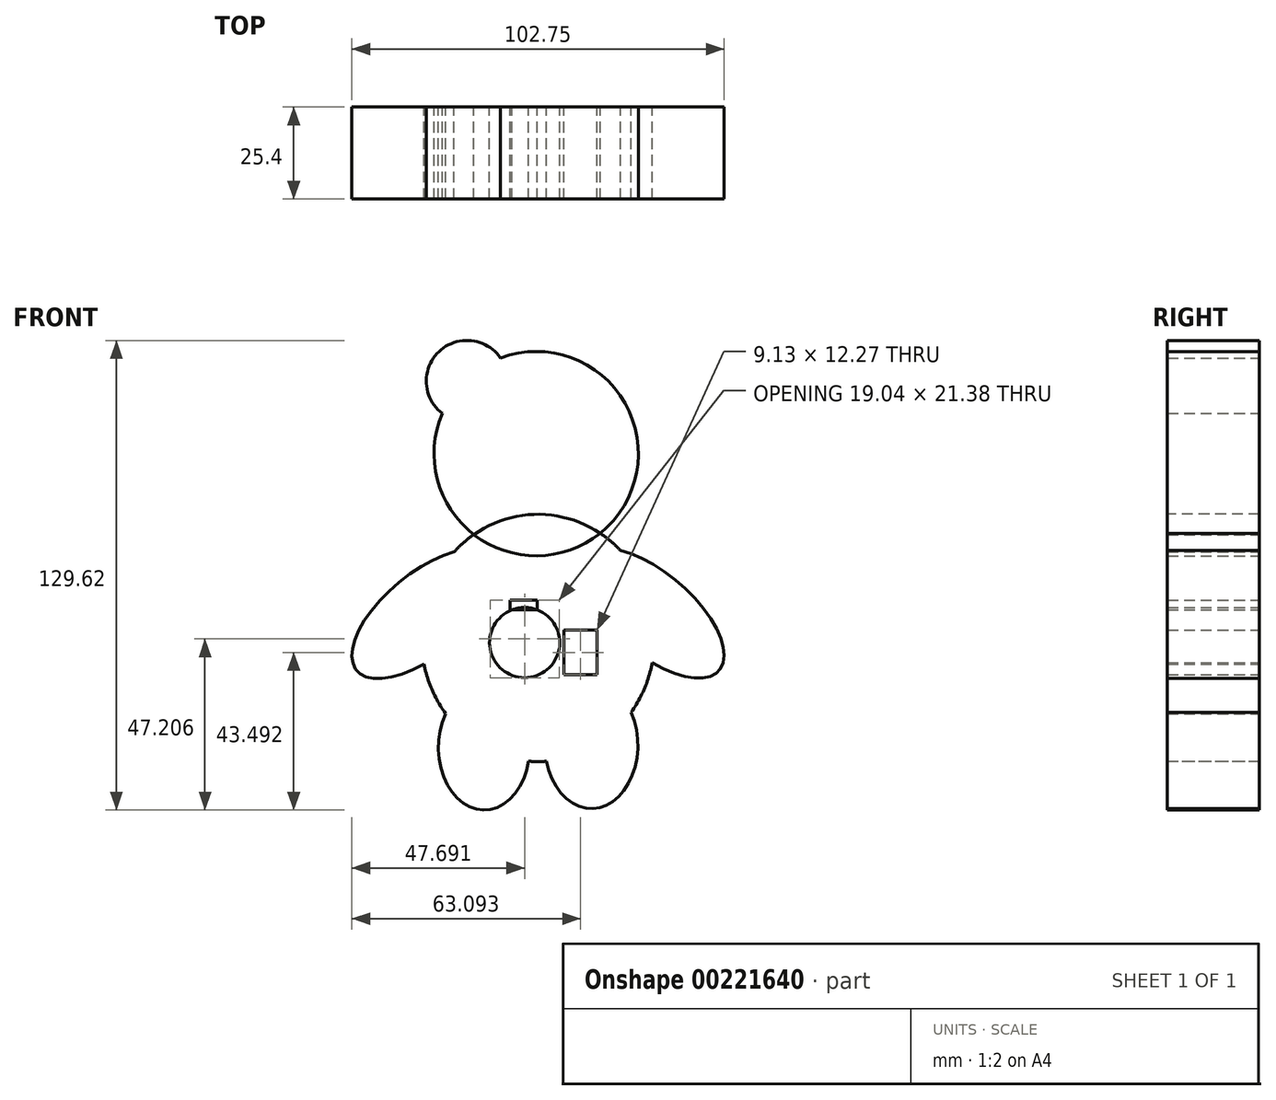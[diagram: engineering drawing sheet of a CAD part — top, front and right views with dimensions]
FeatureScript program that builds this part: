
annotation { "Feature Type Name" : "Feature", "Feature Type Description" : "" }
export const myFeature = defineFeature(function(context is Context, id is Id, definition is map)
    precondition{}
    {
        {
            var Q0;
            Q0=qCreatedBy(makeId("Front.planeOp"),FACE);
            var sketch = newSketch(context, id + "F0", { "sketchPlane" : qUnion([Q0])});
            skCircle(sketch, "E0", {"center": v(3.75, 21.78) * mm, "radius": 28.2 * mm});
            skCircle(sketch, "E1", {"center": v(-15.3, 41.8) * mm, "radius": 11.24 * mm});
            skCircle(sketch, "E2", {"center": v(21.86, 40.85) * mm, "radius": 11.48 * mm});
            skEllipse(sketch, "E3", {"center": v(4.25, -29.08) * mm, "majorRadius": 34.13 * mm, "minorRadius": 32.2 * mm, "majorAxis": v(0, -1)});
            skEllipse(sketch, "E4", {"center": v(-10.63, -59.35) * mm, "majorRadius": 17.23 * mm, "minorRadius": 12.63 * mm, "majorAxis": v(0, -1)});
            skEllipse(sketch, "E5", {"center": v(19, -58.66) * mm, "majorRadius": 17.51 * mm, "minorRadius": 12.83 * mm, "majorAxis": v(0, -1)});
            skEllipse(sketch, "E6", {"center": v(-26.89, -22.46) * mm, "majorRadius": 24.5 * mm, "minorRadius": 11.3 * mm, "majorAxis": v(-0.77, -0.64)});
            skEllipse(sketch, "E7", {"center": v(35.87, -22.32) * mm, "majorRadius": 24.19 * mm, "minorRadius": 11.16 * mm, "majorAxis": v(-0.76, 0.65)});
            skCircle(sketch, "E8", {"center": v(0.57, -30.38) * mm, "radius": 9.69 * mm});
            skLineSegment(sketch, "E9.bottom", {"start": v(-3.42, -18.68) * mm, "end": v(4.07, -18.68) * mm});
            skLineSegment(sketch, "E9.top", {"start": v(-3.42, -21.35) * mm, "end": v(4.07, -21.35) * mm});
            skLineSegment(sketch, "E9.left", {"start": v(-3.42, -18.68) * mm, "end": v(-3.42, -21.35) * mm});
            skLineSegment(sketch, "E9.right", {"start": v(4.07, -18.68) * mm, "end": v(4.07, -21.35) * mm});
            skFitSpline(sketch, "E10", {"points": [v(0, -18.68) * mm, v(4.07, -12.7) * mm, v(9.7, -12.98) * mm], "startDerivative": vector(6.5, 14.43) * mm, "endDerivative": vector(13.03, -3.4) * mm});
            skLineSegment(sketch, "E11.bottom", {"start": v(11.4, -26.96) * mm, "end": v(20.54, -26.96) * mm});
            skLineSegment(sketch, "E11.top", {"start": v(11.4, -39.22) * mm, "end": v(20.54, -39.22) * mm});
            skLineSegment(sketch, "E11.left", {"start": v(11.4, -26.96) * mm, "end": v(11.4, -39.22) * mm});
            skLineSegment(sketch, "E11.right", {"start": v(20.54, -26.96) * mm, "end": v(20.54, -39.22) * mm});
            skPoint(sketch, "E12.1.internal.snap0", {"position": v(0.32, -21.35) * mm});
            skPoint(sketch, "E12.2.internal.snap0", {"position": v(0.32, -21.35) * mm});
            skPoint(sketch, "E12.3.internal.snap0", {"position": v(0.32, -21.35) * mm});
            skPoint(sketch, "E12.4.internal.snap0", {"position": v(0.32, -21.35) * mm});
            skFitSpline(sketch, "E12", {"points": [v(7.7, -23.82) * mm, v(9.98, -21.35) * mm, v(12.27, -21.35) * mm, v(13.4, -21.35) * mm, v(13.7, -21.35) * mm], "startDerivative": vector(5.66, 8.66) * mm, "endDerivative": vector(2.27, -0.06) * mm});
            skFitSpline(sketch, "E13", {"points": [v(14.83, -23.82) * mm, v(15.97, -26.96) * mm], "startDerivative": vector(1.14, -3.14) * mm, "endDerivative": vector(1.14, -3.14) * mm});
            skSolve(sketch);
        }
        {
            var Q0;
            {var subQ1=sQuery(id+"F0.wireOp",EDGE,"E0");var subQ7=sQuery(id+"F0.wireOp",EDGE,"E2");var subQ9=makeQuery(id+"F0.imprint","INTERSECT",VERTEX,{"disambiguationData":[OD(0.0)],"derivedFrom":[subQ1,subQ7]});Q0=makeQuery(id+"F0.imprint","IMPRINT",FACE,{"disambiguationData":[TD([[makeQuery(id+"F0.imprint","IMPRINT",EDGE,{"disambiguationData":[TD([[subQ9,-1.0]])],"derivedFrom":subQ1}),1.0]])]});}
            var Q1;
            {var subQ0=sQuery(id+"F0.wireOp",EDGE,"E4");var subQ1=sQuery(id+"F0.wireOp",EDGE,"E3");var subQ2=makeQuery(id+"F0.imprint","INTERSECT",VERTEX,{"disambiguationData":[OD(0.0)],"derivedFrom":[subQ1,subQ0]});Q1=makeQuery(id+"F0.imprint","IMPRINT",FACE,{"disambiguationData":[TD([[makeQuery(id+"F0.imprint","IMPRINT",EDGE,{"disambiguationData":[TD([[subQ2,-1.0]])],"derivedFrom":subQ1}),1.0]])]});}
            var Q2;
            {var subQ0=sQuery(id+"F0.wireOp",EDGE,"E2");var subQ1=sQuery(id+"F0.wireOp",EDGE,"E0");var subQ2=makeQuery(id+"F0.imprint","INTERSECT",VERTEX,{"disambiguationData":[OD(0.0)],"derivedFrom":[subQ1,subQ0]});Q2=makeQuery(id+"F0.imprint","IMPRINT",FACE,{"disambiguationData":[TD([[makeQuery(id+"F0.imprint","IMPRINT",EDGE,{"disambiguationData":[TD([[subQ2,1.0]])],"derivedFrom":subQ1}),-1.0]])]});}
            var Q3;
            {var subQ0=sQuery(id+"F0.wireOp",EDGE,"E1");var subQ1=sQuery(id+"F0.wireOp",EDGE,"E0");var subQ2=makeQuery(id+"F0.imprint","INTERSECT",VERTEX,{"disambiguationData":[OD(0.0)],"derivedFrom":[subQ1,subQ0]});Q3=makeQuery(id+"F0.imprint","IMPRINT",FACE,{"disambiguationData":[TD([[makeQuery(id+"F0.imprint","IMPRINT",EDGE,{"disambiguationData":[TD([[subQ2,-1.0]])],"derivedFrom":subQ1}),-1.0]])]});}
            var Q4;
            {var subQ0=sQuery(id+"F0.wireOp",EDGE,"E5");var subQ1=sQuery(id+"F0.wireOp",EDGE,"E3");var subQ2=makeQuery(id+"F0.imprint","INTERSECT",VERTEX,{"disambiguationData":[OD(0.0)],"derivedFrom":[subQ1,subQ0]});Q4=makeQuery(id+"F0.imprint","IMPRINT",FACE,{"disambiguationData":[TD([[makeQuery(id+"F0.imprint","IMPRINT",EDGE,{"disambiguationData":[TD([[subQ2,1.0]])],"derivedFrom":subQ1}),-1.0]])]});}
            var Q5;
            {var subQ0=sQuery(id+"F0.wireOp",EDGE,"E4");var subQ1=sQuery(id+"F0.wireOp",EDGE,"E3");var subQ2=makeQuery(id+"F0.imprint","INTERSECT",VERTEX,{"disambiguationData":[OD(0.0)],"derivedFrom":[subQ1,subQ0]});Q5=makeQuery(id+"F0.imprint","IMPRINT",FACE,{"disambiguationData":[TD([[makeQuery(id+"F0.imprint","IMPRINT",EDGE,{"disambiguationData":[TD([[subQ2,-1.0]])],"derivedFrom":subQ1}),-1.0]])]});}
            var Q6;
            {var subQ0=sQuery(id+"F0.wireOp",EDGE,"E2");var subQ1=sQuery(id+"F0.wireOp",EDGE,"E0");var subQ2=makeQuery(id+"F0.imprint","INTERSECT",VERTEX,{"disambiguationData":[OD(0.0)],"derivedFrom":[subQ1,subQ0]});Q6=makeQuery(id+"F0.imprint","IMPRINT",FACE,{"disambiguationData":[TD([[makeQuery(id+"F0.imprint","IMPRINT",EDGE,{"disambiguationData":[TD([[subQ2,1.0]])],"derivedFrom":subQ1}),1.0]])]});}
            var Q7;
            {var subQ0=sQuery(id+"F0.wireOp",EDGE,"E1");var subQ1=sQuery(id+"F0.wireOp",EDGE,"E0");var subQ2=makeQuery(id+"F0.imprint","INTERSECT",VERTEX,{"disambiguationData":[OD(0.0)],"derivedFrom":[subQ1,subQ0]});Q7=makeQuery(id+"F0.imprint","IMPRINT",FACE,{"disambiguationData":[TD([[makeQuery(id+"F0.imprint","IMPRINT",EDGE,{"disambiguationData":[TD([[subQ2,-1.0]])],"derivedFrom":subQ1}),1.0]])]});}
            var Q8;
            {var subQ0=sQuery(id+"F0.wireOp",EDGE,"E3");var subQ1=sQuery(id+"F0.wireOp",EDGE,"E0");var subQ2=makeQuery(id+"F0.imprint","INTERSECT",VERTEX,{"disambiguationData":[OD(0.0)],"derivedFrom":[subQ1,subQ0]});Q8=makeQuery(id+"F0.imprint","IMPRINT",FACE,{"disambiguationData":[TD([[makeQuery(id+"F0.imprint","IMPRINT",EDGE,{"disambiguationData":[TD([[subQ2,-1.0]])],"derivedFrom":subQ1}),1.0]])]});}
            var Q9;
            {var subQ0=sQuery(id+"F0.wireOp",EDGE,"E5");var subQ1=sQuery(id+"F0.wireOp",EDGE,"E3");var subQ2=makeQuery(id+"F0.imprint","INTERSECT",VERTEX,{"disambiguationData":[OD(0.0)],"derivedFrom":[subQ1,subQ0]});Q9=makeQuery(id+"F0.imprint","IMPRINT",FACE,{"disambiguationData":[TD([[makeQuery(id+"F0.imprint","IMPRINT",EDGE,{"disambiguationData":[TD([[subQ2,1.0]])],"derivedFrom":subQ1}),1.0]])]});}
            var Q10;
            {var subQ0=sQuery(id+"F0.wireOp",EDGE,"E7");var subQ1=sQuery(id+"F0.wireOp",EDGE,"E3");var subQ2=makeQuery(id+"F0.imprint","INTERSECT",VERTEX,{"disambiguationData":[OD(0.0)],"derivedFrom":[subQ1,subQ0]});Q10=makeQuery(id+"F0.imprint","IMPRINT",FACE,{"disambiguationData":[TD([[makeQuery(id+"F0.imprint","IMPRINT",EDGE,{"disambiguationData":[TD([[subQ2,-1.0]])],"derivedFrom":subQ1}),1.0]])]});}
            var Q11;
            {var subQ0=sQuery(id+"F0.wireOp",EDGE,"E6");var subQ1=sQuery(id+"F0.wireOp",EDGE,"E3");var subQ2=makeQuery(id+"F0.imprint","INTERSECT",VERTEX,{"disambiguationData":[OD(0.0)],"derivedFrom":[subQ1,subQ0]});Q11=makeQuery(id+"F0.imprint","IMPRINT",FACE,{"disambiguationData":[TD([[makeQuery(id+"F0.imprint","IMPRINT",EDGE,{"disambiguationData":[TD([[subQ2,-1.0]])],"derivedFrom":subQ1}),1.0]])]});}
            var Q12;
            {var subQ0=sQuery(id+"F0.wireOp",EDGE,"E9.top");var subQ1=sQuery(id+"F0.wireOp",EDGE,"E8");var subQ3=makeQuery(id+"F0.imprint","INTERSECT",VERTEX,{"derivedFrom":[subQ1,subQ0]});Q12=makeQuery(id+"F0.imprint","IMPRINT",FACE,{"disambiguationData":[TD([[makeQuery(id+"F0.imprint","IMPRINT",EDGE,{"disambiguationData":[TD([[subQ3,1.0]])],"derivedFrom":subQ1}),1.0]])]});}
            var Q13;
            {var subQ0=sQuery(id+"F0.wireOp",EDGE,"E6");var subQ1=sQuery(id+"F0.wireOp",EDGE,"E3");var subQ2=makeQuery(id+"F0.imprint","INTERSECT",VERTEX,{"disambiguationData":[OD(0.0)],"derivedFrom":[subQ1,subQ0]});Q13=makeQuery(id+"F0.imprint","IMPRINT",FACE,{"disambiguationData":[TD([[makeQuery(id+"F0.imprint","IMPRINT",EDGE,{"disambiguationData":[TD([[subQ2,-1.0]])],"derivedFrom":subQ1}),-1.0]])]});}
            var Q14;
            {var subQ0=sQuery(id+"F0.wireOp",EDGE,"E7");var subQ1=sQuery(id+"F0.wireOp",EDGE,"E3");var subQ2=makeQuery(id+"F0.imprint","INTERSECT",VERTEX,{"disambiguationData":[OD(0.0)],"derivedFrom":[subQ1,subQ0]});Q14=makeQuery(id+"F0.imprint","IMPRINT",FACE,{"disambiguationData":[TD([[makeQuery(id+"F0.imprint","IMPRINT",EDGE,{"disambiguationData":[TD([[subQ2,-1.0]])],"derivedFrom":subQ1}),-1.0]])]});}
            var Q15;
            {var subQ24=sQuery(id+"F0.wireOp",EDGE,"E9.left");Q15=makeQuery(id+"F0.imprint","IMPRINT",FACE,{"disambiguationData":[TD([[makeQuery(id+"F0.imprint","IMPRINT",EDGE,{"derivedFrom":subQ24}),-1.0]])]});}
            extrude(context, id + "F1", {"entities" : qUnion([Q0, Q1, Q2, Q3, Q4, Q5, Q6, Q7, Q8, Q9, Q10, Q11, Q12, Q13, Q14, Q15]), "endBound" : BoundingType.SYMMETRIC, "depth" : 25.4 * mm});
        }
    });
